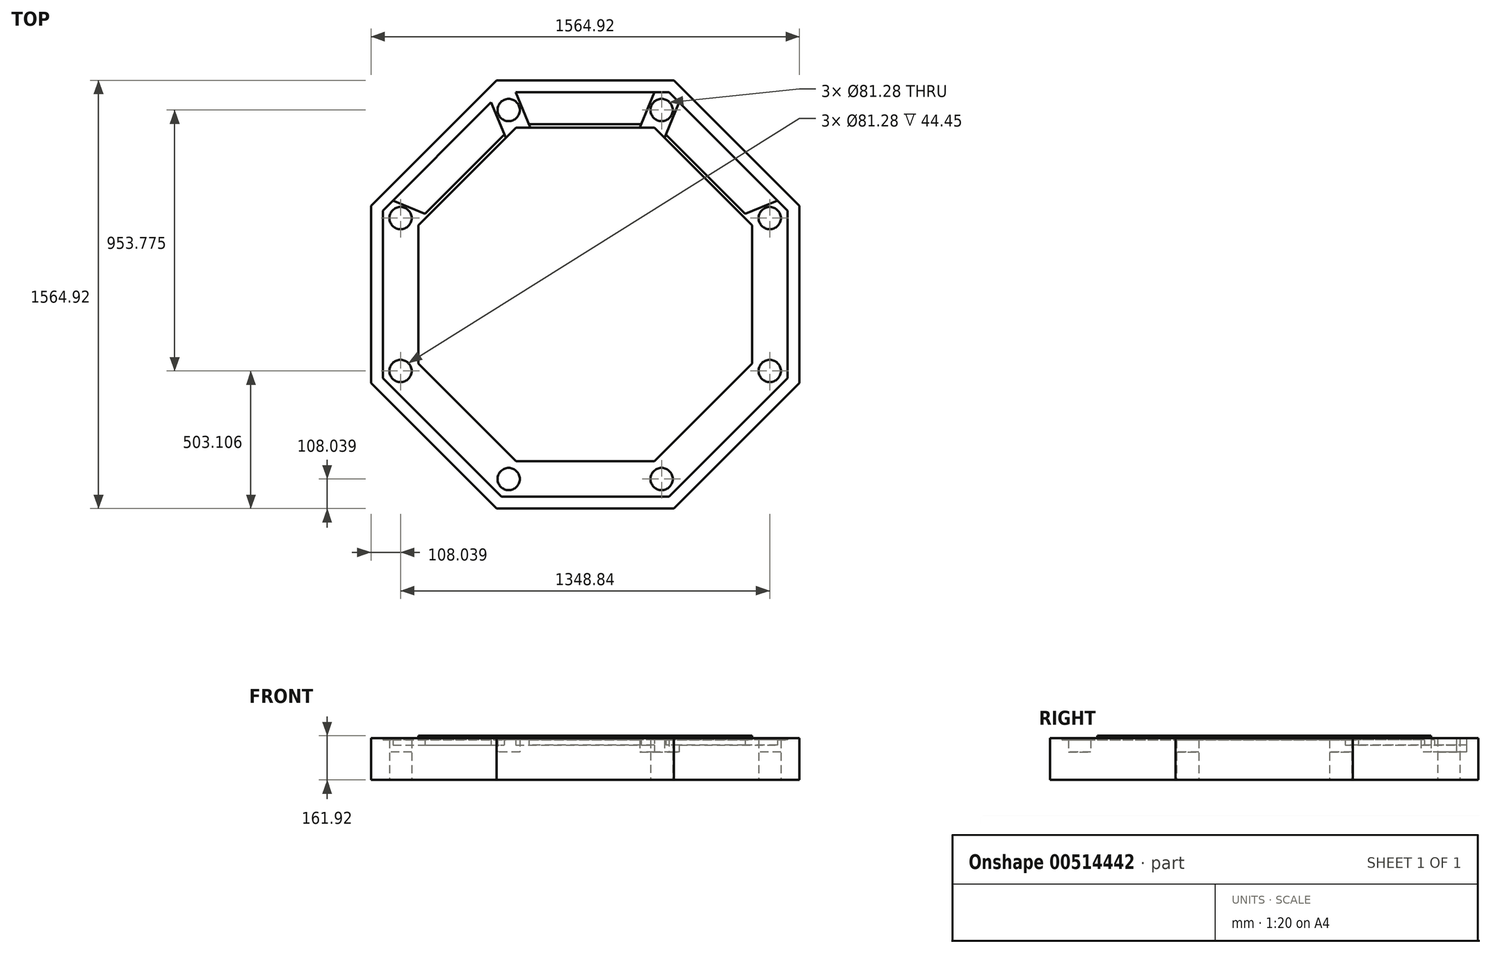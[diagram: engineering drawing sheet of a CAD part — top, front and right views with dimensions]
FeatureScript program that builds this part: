
annotation { "Feature Type Name" : "Feature", "Feature Type Description" : "" }
export const myFeature = defineFeature(function(context is Context, id is Id, definition is map)
    precondition{}
    {
        {
            var Q0;
            Q0=qCreatedBy(makeId("Top.planeOp"),FACE);
            var sketch = newSketch(context, id + "F0", { "sketchPlane" : qUnion([Q0])});
            skLineSegment(sketch, "E0.0", {"start": v(-324.1, 782.46) * mm, "end": v(324.1, 782.46) * mm});
            skLineSegment(sketch, "E0.1", {"start": v(324.1, 782.46) * mm, "end": v(782.46, 324.1) * mm});
            skLineSegment(sketch, "E0.2", {"start": v(782.46, 324.1) * mm, "end": v(782.46, -324.1) * mm});
            skLineSegment(sketch, "E0.3", {"start": v(782.46, -324.1) * mm, "end": v(324.1, -782.46) * mm});
            skLineSegment(sketch, "E0.4", {"start": v(324.1, -782.46) * mm, "end": v(-324.1, -782.46) * mm});
            skLineSegment(sketch, "E0.5", {"start": v(-324.1, -782.46) * mm, "end": v(-782.46, -324.1) * mm});
            skLineSegment(sketch, "E0.6", {"start": v(-782.46, -324.1) * mm, "end": v(-782.46, 324.1) * mm});
            skLineSegment(sketch, "E0.7", {"start": v(-782.46, 324.1) * mm, "end": v(-324.1, 782.46) * mm});
            skPoint(sketch, "E0.0.midPoint", {"position": v(0, 782.46) * mm});
            skLineSegment(sketch, "E1.0", {"start": v(-252.5, 609.6) * mm, "end": v(252.5, 609.6) * mm});
            skLineSegment(sketch, "E1.1", {"start": v(252.5, 609.6) * mm, "end": v(609.6, 252.5) * mm});
            skLineSegment(sketch, "E1.2", {"start": v(609.6, 252.5) * mm, "end": v(609.6, -252.5) * mm});
            skLineSegment(sketch, "E1.3", {"start": v(609.6, -252.5) * mm, "end": v(252.5, -609.6) * mm});
            skLineSegment(sketch, "E1.4", {"start": v(252.5, -609.6) * mm, "end": v(-252.5, -609.6) * mm});
            skLineSegment(sketch, "E1.5", {"start": v(-252.5, -609.6) * mm, "end": v(-609.6, -252.5) * mm});
            skLineSegment(sketch, "E1.6", {"start": v(-609.6, -252.5) * mm, "end": v(-609.6, 252.5) * mm});
            skLineSegment(sketch, "E1.7", {"start": v(-609.6, 252.5) * mm, "end": v(-252.5, 609.6) * mm});
            skPoint(sketch, "E1.0.midPoint", {"position": v(0, 609.6) * mm});
            skLineSegment(sketch, "E2.0", {"start": v(-306.2, 739.24) * mm, "end": v(306.2, 739.24) * mm});
            skLineSegment(sketch, "E2.1", {"start": v(306.2, 739.24) * mm, "end": v(739.24, 306.2) * mm});
            skLineSegment(sketch, "E2.2", {"start": v(739.24, 306.2) * mm, "end": v(739.24, -306.2) * mm});
            skLineSegment(sketch, "E2.3", {"start": v(739.24, -306.2) * mm, "end": v(306.2, -739.24) * mm});
            skLineSegment(sketch, "E2.4", {"start": v(306.2, -739.24) * mm, "end": v(-306.2, -739.24) * mm});
            skLineSegment(sketch, "E2.5", {"start": v(-306.2, -739.24) * mm, "end": v(-739.24, -306.2) * mm});
            skLineSegment(sketch, "E2.6", {"start": v(-739.24, -306.2) * mm, "end": v(-739.24, 306.2) * mm});
            skLineSegment(sketch, "E2.7", {"start": v(-739.24, 306.2) * mm, "end": v(-306.2, 739.24) * mm});
            skPoint(sketch, "E2.0.midPoint", {"position": v(0, 739.24) * mm});
            skLineSegment(sketch, "E3", {"start": v(-306.2, 739.24) * mm, "end": v(-252.5, 609.6) * mm, "construction": true});
            skLineSegment(sketch, "E4.0", {"start": v(-253.58, 739.24) * mm, "end": v(-199.88, 609.6) * mm});
            skLineSegment(sketch, "E5.0", {"start": v(-343.41, 702.03) * mm, "end": v(-289.71, 572.4) * mm});
            skLineSegment(sketch, "E6", {"start": v(0, 782.46) * mm, "end": v(0, -782.46) * mm, "construction": true});
            skCircle(sketch, "E7", {"center": v(-279.35, 674.42) * mm, "radius": 40.64 * mm});
            skLineSegment(sketch, "E8.MirrorCS", {"start": v(253.58, 739.24) * mm, "end": v(199.88, 609.6) * mm});
            skLineSegment(sketch, "E9.MirrorCS", {"start": v(343.41, 702.03) * mm, "end": v(289.71, 572.4) * mm});
            skCircle(sketch, "E10.MirrorC", {"center": v(279.35, 674.42) * mm, "radius": 40.64 * mm});
            skLineSegment(sketch, "E11", {"start": v(-782.46, 0) * mm, "end": v(782.46, 0) * mm, "construction": true});
            skLineSegment(sketch, "E12.MirrorCS", {"start": v(343.41, -702.03) * mm, "end": v(289.71, -572.4) * mm});
            skLineSegment(sketch, "E13.MirrorCS", {"start": v(253.58, -739.24) * mm, "end": v(199.88, -609.6) * mm});
            skCircle(sketch, "E14.MirrorC", {"center": v(279.35, -674.42) * mm, "radius": 40.64 * mm});
            skCircle(sketch, "E15.MirrorC", {"center": v(-279.35, -674.42) * mm, "radius": 40.64 * mm});
            skLineSegment(sketch, "E16.MirrorCS", {"start": v(-253.58, -739.24) * mm, "end": v(-199.88, -609.6) * mm});
            skLineSegment(sketch, "E17.MirrorCS", {"start": v(-343.41, -702.03) * mm, "end": v(-289.71, -572.4) * mm});
            skLineSegment(sketch, "E18", {"start": v(553.28, -553.28) * mm, "end": v(-553.28, 553.28) * mm, "construction": true});
            skLineSegment(sketch, "E19", {"start": v(553.28, 553.28) * mm, "end": v(-553.28, -553.28) * mm, "construction": true});
            skLineSegment(sketch, "E20.MirrorCS", {"start": v(702.03, 343.41) * mm, "end": v(572.4, 289.71) * mm});
            skLineSegment(sketch, "E21.MirrorCS", {"start": v(739.24, 253.58) * mm, "end": v(609.6, 199.88) * mm});
            skCircle(sketch, "E22.MirrorC", {"center": v(674.42, 279.35) * mm, "radius": 40.64 * mm});
            skLineSegment(sketch, "E23.MirrorCS", {"start": v(-739.24, -253.58) * mm, "end": v(-609.6, -199.88) * mm});
            skCircle(sketch, "E24.MirrorC", {"center": v(-674.42, -279.35) * mm, "radius": 40.64 * mm});
            skLineSegment(sketch, "E25.MirrorCS", {"start": v(-702.03, -343.41) * mm, "end": v(-572.4, -289.71) * mm});
            skLineSegment(sketch, "E26.MirrorCS", {"start": v(702.03, -343.41) * mm, "end": v(572.4, -289.71) * mm});
            skLineSegment(sketch, "E27.MirrorCS", {"start": v(739.24, -253.58) * mm, "end": v(609.6, -199.88) * mm});
            skCircle(sketch, "E28.MirrorC", {"center": v(674.42, -279.35) * mm, "radius": 40.64 * mm});
            skLineSegment(sketch, "E29.MirrorCS", {"start": v(-702.03, 343.41) * mm, "end": v(-572.4, 289.71) * mm});
            skLineSegment(sketch, "E30.MirrorCS", {"start": v(-739.24, 253.58) * mm, "end": v(-609.6, 199.88) * mm});
            skCircle(sketch, "E31.MirrorC", {"center": v(-674.42, 279.35) * mm, "radius": 40.64 * mm});
            skLineSegment(sketch, "E32.0", {"start": v(-205.14, 622.3) * mm, "end": v(205.14, 622.3) * mm});
            skLineSegment(sketch, "E33.MirrorCS", {"start": v(-205.14, -622.3) * mm, "end": v(205.14, -622.3) * mm});
            skLineSegment(sketch, "E34.MirrorCS", {"start": v(-622.3, -205.14) * mm, "end": v(-622.3, 205.14) * mm});
            skLineSegment(sketch, "E35.MirrorCS", {"start": v(622.3, -205.14) * mm, "end": v(622.3, 205.14) * mm});
            skLineSegment(sketch, "E36.0", {"start": v(294.97, 585.1) * mm, "end": v(585.1, 294.97) * mm});
            skLineSegment(sketch, "E37.MirrorCS", {"start": v(-585.1, -294.97) * mm, "end": v(-294.97, -585.1) * mm});
            skLineSegment(sketch, "E38.MirrorCS", {"start": v(-294.97, 585.1) * mm, "end": v(-585.1, 294.97) * mm});
            skLineSegment(sketch, "E39.MirrorCS", {"start": v(585.1, -294.97) * mm, "end": v(294.97, -585.1) * mm});
            skLineSegment(sketch, "E40", {"start": v(-585.1, 294.97) * mm, "end": v(-585.1, 294.97) * mm});
            skLineSegment(sketch, "E41", {"start": v(622.3, -205.14) * mm, "end": v(622.26, -205.13) * mm});
            skSolve(sketch);
        }
        {
            var Q0;
            Q0=makeQuery(id+"F0.imprint","IMPRINT",FACE,{"disambiguationData":[TD([[makeQuery(id+"F0.imprint","IMPRINT",EDGE,{"derivedFrom":sQuery(id+"F0.wireOp",EDGE,"E0.0")}),-1.0]])]});
            extrude(context, id + "F1", {"entities" : qUnion([Q0]), "endBound" : BoundingType.SYMMETRIC, "depth" : 152.4 * mm, "offsetDistance" : 25.4 * mm});
        }
        {
            var Q0;
            {var subQ0=sQuery(id+"F0.wireOp",EDGE,"E5.0");Q0=makeQuery(id+"F0.imprint","IMPRINT",FACE,{"disambiguationData":[TD([[makeQuery(id+"F0.imprint","IMPRINT",EDGE,{"derivedFrom":subQ0}),-1.0]])]});}
            var Q1;
            {var subQ0=sQuery(id+"F0.wireOp",EDGE,"E4.0");Q1=makeQuery(id+"F0.imprint","IMPRINT",FACE,{"disambiguationData":[TD([[makeQuery(id+"F0.imprint","IMPRINT",EDGE,{"derivedFrom":subQ0}),1.0]])]});}
            var Q2;
            {var subQ0=sQuery(id+"F0.wireOp",EDGE,"E9.MirrorCS");Q2=makeQuery(id+"F0.imprint","IMPRINT",FACE,{"disambiguationData":[TD([[makeQuery(id+"F0.imprint","IMPRINT",EDGE,{"derivedFrom":subQ0}),1.0]])]});}
            var Q3;
            {var subQ0=sQuery(id+"F0.wireOp",EDGE,"E23.MirrorCS");Q3=makeQuery(id+"F0.imprint","IMPRINT",FACE,{"disambiguationData":[TD([[makeQuery(id+"F0.imprint","IMPRINT",EDGE,{"derivedFrom":subQ0}),1.0]])]});}
            var Q4;
            {var subQ0=sQuery(id+"F0.wireOp",EDGE,"E21.MirrorCS");Q4=makeQuery(id+"F0.imprint","IMPRINT",FACE,{"disambiguationData":[TD([[makeQuery(id+"F0.imprint","IMPRINT",EDGE,{"derivedFrom":subQ0}),1.0]])]});}
            var Q5;
            {var subQ0=sQuery(id+"F0.wireOp",EDGE,"E12.MirrorCS");Q5=makeQuery(id+"F0.imprint","IMPRINT",FACE,{"disambiguationData":[TD([[makeQuery(id+"F0.imprint","IMPRINT",EDGE,{"derivedFrom":subQ0}),-1.0]])]});}
            var Q6;
            {var subQ0=sQuery(id+"F0.wireOp",EDGE,"E13.MirrorCS");Q6=makeQuery(id+"F0.imprint","IMPRINT",FACE,{"disambiguationData":[TD([[makeQuery(id+"F0.imprint","IMPRINT",EDGE,{"derivedFrom":subQ0}),1.0]])]});}
            var Q7;
            {var subQ0=sQuery(id+"F0.wireOp",EDGE,"E17.MirrorCS");Q7=makeQuery(id+"F0.imprint","IMPRINT",FACE,{"disambiguationData":[TD([[makeQuery(id+"F0.imprint","IMPRINT",EDGE,{"derivedFrom":subQ0}),1.0]])]});}
            extrude(context, id + "F2", {"entities" : qUnion([Q0, Q1, Q2, Q3, Q4, Q5, Q6, Q7]), "operationType" : NewBodyOperationType.ADD, "endBound" : BoundingType.SYMMETRIC, "depth" : 127 * mm});
        }
        {
            var Q0;
            Q0=makeQuery(id+"F2.opExtrude","CAP_FACE",FACE,{"disambiguationData":[OSD([sQuery(id+"F0.wireOp",EDGE,"E1.3"),sQuery(id+"F0.wireOp",EDGE,"E2.3"),sQuery(id+"F0.wireOp",EDGE,"E12.MirrorCS"),sQuery(id+"F0.wireOp",EDGE,"E26.MirrorCS")])],"isStart":true});
            var Q1;
            Q1=makeQuery(id+"F2.opExtrude","CAP_FACE",FACE,{"disambiguationData":[OSD([sQuery(id+"F0.wireOp",EDGE,"E1.4"),sQuery(id+"F0.wireOp",EDGE,"E2.4"),sQuery(id+"F0.wireOp",EDGE,"E13.MirrorCS"),sQuery(id+"F0.wireOp",EDGE,"E16.MirrorCS")])],"isStart":true});
            var Q2;
            Q2=makeQuery(id+"F2.opExtrude","CAP_FACE",FACE,{"disambiguationData":[OSD([sQuery(id+"F0.wireOp",EDGE,"E1.5"),sQuery(id+"F0.wireOp",EDGE,"E2.5"),sQuery(id+"F0.wireOp",EDGE,"E17.MirrorCS"),sQuery(id+"F0.wireOp",EDGE,"E25.MirrorCS")])],"isStart":true});
            var Q3;
            Q3=makeQuery(id+"F2.opExtrude","CAP_FACE",FACE,{"disambiguationData":[OSD([sQuery(id+"F0.wireOp",EDGE,"E1.6"),sQuery(id+"F0.wireOp",EDGE,"E2.6"),sQuery(id+"F0.wireOp",EDGE,"E23.MirrorCS"),sQuery(id+"F0.wireOp",EDGE,"E30.MirrorCS")])],"isStart":true});
            var Q4;
            Q4=makeQuery(id+"F2.opExtrude","CAP_FACE",FACE,{"disambiguationData":[OSD([sQuery(id+"F0.wireOp",EDGE,"E1.7"),sQuery(id+"F0.wireOp",EDGE,"E2.7"),sQuery(id+"F0.wireOp",EDGE,"E5.0"),sQuery(id+"F0.wireOp",EDGE,"E29.MirrorCS")])],"isStart":true});
            var Q5;
            Q5=makeQuery(id+"F2.opExtrude","CAP_FACE",FACE,{"disambiguationData":[OSD([sQuery(id+"F0.wireOp",EDGE,"E1.0"),sQuery(id+"F0.wireOp",EDGE,"E2.0"),sQuery(id+"F0.wireOp",EDGE,"E4.0"),sQuery(id+"F0.wireOp",EDGE,"E8.MirrorCS")])],"isStart":true});
            var Q6;
            Q6=makeQuery(id+"F2.opExtrude","CAP_FACE",FACE,{"disambiguationData":[OSD([sQuery(id+"F0.wireOp",EDGE,"E1.1"),sQuery(id+"F0.wireOp",EDGE,"E2.1"),sQuery(id+"F0.wireOp",EDGE,"E9.MirrorCS"),sQuery(id+"F0.wireOp",EDGE,"E20.MirrorCS")])],"isStart":true});
            var Q7;
            Q7=makeQuery(id+"F2.opExtrude","CAP_FACE",FACE,{"disambiguationData":[OSD([sQuery(id+"F0.wireOp",EDGE,"E1.2"),sQuery(id+"F0.wireOp",EDGE,"E2.2"),sQuery(id+"F0.wireOp",EDGE,"E21.MirrorCS"),sQuery(id+"F0.wireOp",EDGE,"E27.MirrorCS")])],"isStart":true});
            extrude(context, id + "F3", {"entities" : qUnion([Q0, Q1, Q2, Q3, Q4, Q5, Q6, Q7]), "operationType" : NewBodyOperationType.ADD, "depth" : 12.7 * mm});
        }
        {
            var Q0;
            {var subQ4=sQuery(id+"F0.wireOp",EDGE,"E4.0");Q0=makeQuery(id+"F0.imprint","IMPRINT",FACE,{"disambiguationData":[TD([[makeQuery(id+"F0.imprint","IMPRINT",EDGE,{"derivedFrom":subQ4}),-1.0]])]});}
            var Q1;
            {var subQ3=sQuery(id+"F0.wireOp",EDGE,"E8.MirrorCS");Q1=makeQuery(id+"F0.imprint","IMPRINT",FACE,{"disambiguationData":[TD([[makeQuery(id+"F0.imprint","IMPRINT",EDGE,{"derivedFrom":subQ3}),1.0]])]});}
            var Q2;
            {var subQ7=sQuery(id+"F0.wireOp",EDGE,"E29.MirrorCS");Q2=makeQuery(id+"F0.imprint","IMPRINT",FACE,{"disambiguationData":[TD([[makeQuery(id+"F0.imprint","IMPRINT",EDGE,{"derivedFrom":subQ7}),-1.0]])]});}
            var Q3;
            {var subQ4=sQuery(id+"F0.wireOp",EDGE,"E23.MirrorCS");Q3=makeQuery(id+"F0.imprint","IMPRINT",FACE,{"disambiguationData":[TD([[makeQuery(id+"F0.imprint","IMPRINT",EDGE,{"derivedFrom":subQ4}),-1.0]])]});}
            var Q4;
            {var subQ3=sQuery(id+"F0.wireOp",EDGE,"E20.MirrorCS");Q4=makeQuery(id+"F0.imprint","IMPRINT",FACE,{"disambiguationData":[TD([[makeQuery(id+"F0.imprint","IMPRINT",EDGE,{"derivedFrom":subQ3}),1.0]])]});}
            var Q5;
            {var subQ7=sQuery(id+"F0.wireOp",EDGE,"E26.MirrorCS");Q5=makeQuery(id+"F0.imprint","IMPRINT",FACE,{"disambiguationData":[TD([[makeQuery(id+"F0.imprint","IMPRINT",EDGE,{"derivedFrom":subQ7}),-1.0]])]});}
            var Q6;
            Q6=makeQuery(id+"F0.imprint","IMPRINT",FACE,{"disambiguationData":[TD([[makeQuery(id+"F0.imprint","IMPRINT",EDGE,{"derivedFrom":sQuery(id+"F0.wireOp",EDGE,"E15.MirrorC")}),1.0]])]});
            var Q7;
            {var subQ3=sQuery(id+"F0.wireOp",EDGE,"E12.MirrorCS");Q7=makeQuery(id+"F0.imprint","IMPRINT",FACE,{"disambiguationData":[TD([[makeQuery(id+"F0.imprint","IMPRINT",EDGE,{"derivedFrom":subQ3}),1.0]])]});}
            var Q8;
            Q8=makeQuery(id+"F0.imprint","IMPRINT",FACE,{"disambiguationData":[TD([[makeQuery(id+"F0.imprint","IMPRINT",EDGE,{"derivedFrom":sQuery(id+"F0.wireOp",EDGE,"E22.MirrorC")}),1.0]])]});
            var Q9;
            Q9=makeQuery(id+"F0.imprint","IMPRINT",FACE,{"disambiguationData":[TD([[makeQuery(id+"F0.imprint","IMPRINT",EDGE,{"derivedFrom":sQuery(id+"F0.wireOp",EDGE,"E10.MirrorC")}),-1.0]])]});
            var Q10;
            Q10=makeQuery(id+"F0.imprint","IMPRINT",FACE,{"disambiguationData":[TD([[makeQuery(id+"F0.imprint","IMPRINT",EDGE,{"derivedFrom":sQuery(id+"F0.wireOp",EDGE,"E7")}),1.0]])]});
            var Q11;
            Q11=makeQuery(id+"F0.imprint","IMPRINT",FACE,{"disambiguationData":[TD([[makeQuery(id+"F0.imprint","IMPRINT",EDGE,{"derivedFrom":sQuery(id+"F0.wireOp",EDGE,"E31.MirrorC")}),-1.0]])]});
            var Q12;
            Q12=makeQuery(id+"F0.imprint","IMPRINT",FACE,{"disambiguationData":[TD([[makeQuery(id+"F0.imprint","IMPRINT",EDGE,{"derivedFrom":sQuery(id+"F0.wireOp",EDGE,"E24.MirrorC")}),1.0]])]});
            var Q13;
            Q13=makeQuery(id+"F0.imprint","IMPRINT",FACE,{"disambiguationData":[TD([[makeQuery(id+"F0.imprint","IMPRINT",EDGE,{"derivedFrom":sQuery(id+"F0.wireOp",EDGE,"E15.MirrorC")}),-1.0]])]});
            var Q14;
            Q14=makeQuery(id+"F0.imprint","IMPRINT",FACE,{"disambiguationData":[TD([[makeQuery(id+"F0.imprint","IMPRINT",EDGE,{"derivedFrom":sQuery(id+"F0.wireOp",EDGE,"E14.MirrorC")}),1.0]])]});
            var Q15;
            Q15=makeQuery(id+"F0.imprint","IMPRINT",FACE,{"disambiguationData":[TD([[makeQuery(id+"F0.imprint","IMPRINT",EDGE,{"derivedFrom":sQuery(id+"F0.wireOp",EDGE,"E28.MirrorC")}),-1.0]])]});
            extrude(context, id + "F4", {"entities" : qUnion([Q0, Q1, Q2, Q3, Q4, Q5, Q6, Q7, Q8, Q9, Q10, Q11, Q12, Q13, Q14, Q15]), "operationType" : NewBodyOperationType.ADD, "endBound" : BoundingType.SYMMETRIC, "depth" : 152.4 * mm});
        }
        {
            var Q0;
            Q0=makeQuery(id+"F0.imprint","IMPRINT",FACE,{"disambiguationData":[TD([[makeQuery(id+"F0.imprint","IMPRINT",EDGE,{"derivedFrom":sQuery(id+"F0.wireOp",EDGE,"E31.MirrorC")}),-1.0]])]});
            var Q1;
            Q1=makeQuery(id+"F0.imprint","IMPRINT",FACE,{"disambiguationData":[TD([[makeQuery(id+"F0.imprint","IMPRINT",EDGE,{"derivedFrom":sQuery(id+"F0.wireOp",EDGE,"E7")}),1.0]])]});
            var Q2;
            Q2=makeQuery(id+"F0.imprint","IMPRINT",FACE,{"disambiguationData":[TD([[makeQuery(id+"F0.imprint","IMPRINT",EDGE,{"derivedFrom":sQuery(id+"F0.wireOp",EDGE,"E10.MirrorC")}),-1.0]])]});
            var Q3;
            Q3=makeQuery(id+"F0.imprint","IMPRINT",FACE,{"disambiguationData":[TD([[makeQuery(id+"F0.imprint","IMPRINT",EDGE,{"derivedFrom":sQuery(id+"F0.wireOp",EDGE,"E22.MirrorC")}),1.0]])]});
            var Q4;
            Q4=makeQuery(id+"F0.imprint","IMPRINT",FACE,{"disambiguationData":[TD([[makeQuery(id+"F0.imprint","IMPRINT",EDGE,{"derivedFrom":sQuery(id+"F0.wireOp",EDGE,"E28.MirrorC")}),-1.0]])]});
            var Q5;
            Q5=makeQuery(id+"F0.imprint","IMPRINT",FACE,{"disambiguationData":[TD([[makeQuery(id+"F0.imprint","IMPRINT",EDGE,{"derivedFrom":sQuery(id+"F0.wireOp",EDGE,"E14.MirrorC")}),1.0]])]});
            var Q6;
            Q6=makeQuery(id+"F0.imprint","IMPRINT",FACE,{"disambiguationData":[TD([[makeQuery(id+"F0.imprint","IMPRINT",EDGE,{"derivedFrom":sQuery(id+"F0.wireOp",EDGE,"E15.MirrorC")}),-1.0]])]});
            var Q7;
            Q7=makeQuery(id+"F0.imprint","IMPRINT",FACE,{"disambiguationData":[TD([[makeQuery(id+"F0.imprint","IMPRINT",EDGE,{"derivedFrom":sQuery(id+"F0.wireOp",EDGE,"E24.MirrorC")}),1.0]])]});
            extrude(context, id + "F5", {"entities" : qUnion([Q0, Q1, Q2, Q3, Q4, Q5, Q6, Q7]), "operationType" : NewBodyOperationType.REMOVE, "endBound" : BoundingType.THROUGH_ALL, "depth" : 50.8 * mm});
        }
        {
            var Q0;
            Q0=makeQuery(id+"F0.imprint","IMPRINT",FACE,{"disambiguationData":[TD([[makeQuery(id+"F0.imprint","IMPRINT",EDGE,{"derivedFrom":sQuery(id+"F0.wireOp",EDGE,"E7")}),1.0]])]});
            var Q1;
            Q1=makeQuery(id+"F0.imprint","IMPRINT",FACE,{"disambiguationData":[TD([[makeQuery(id+"F0.imprint","IMPRINT",EDGE,{"derivedFrom":sQuery(id+"F0.wireOp",EDGE,"E10.MirrorC")}),-1.0]])]});
            var Q2;
            Q2=makeQuery(id+"F0.imprint","IMPRINT",FACE,{"disambiguationData":[TD([[makeQuery(id+"F0.imprint","IMPRINT",EDGE,{"derivedFrom":sQuery(id+"F0.wireOp",EDGE,"E22.MirrorC")}),1.0]])]});
            var Q3;
            Q3=makeQuery(id+"F0.imprint","IMPRINT",FACE,{"disambiguationData":[TD([[makeQuery(id+"F0.imprint","IMPRINT",EDGE,{"derivedFrom":sQuery(id+"F0.wireOp",EDGE,"E28.MirrorC")}),-1.0]])]});
            var Q4;
            Q4=makeQuery(id+"F0.imprint","IMPRINT",FACE,{"disambiguationData":[TD([[makeQuery(id+"F0.imprint","IMPRINT",EDGE,{"derivedFrom":sQuery(id+"F0.wireOp",EDGE,"E14.MirrorC")}),1.0]])]});
            var Q5;
            Q5=makeQuery(id+"F0.imprint","IMPRINT",FACE,{"disambiguationData":[TD([[makeQuery(id+"F0.imprint","IMPRINT",EDGE,{"derivedFrom":sQuery(id+"F0.wireOp",EDGE,"E15.MirrorC")}),-1.0]])]});
            var Q6;
            Q6=makeQuery(id+"F0.imprint","IMPRINT",FACE,{"disambiguationData":[TD([[makeQuery(id+"F0.imprint","IMPRINT",EDGE,{"derivedFrom":sQuery(id+"F0.wireOp",EDGE,"E24.MirrorC")}),1.0]])]});
            var Q7;
            Q7=makeQuery(id+"F0.imprint","IMPRINT",FACE,{"disambiguationData":[TD([[makeQuery(id+"F0.imprint","IMPRINT",EDGE,{"derivedFrom":sQuery(id+"F0.wireOp",EDGE,"E31.MirrorC")}),-1.0]])]});
            extrude(context, id + "F6", {"entities" : qUnion([Q0, Q1, Q2, Q3, Q4, Q5, Q6, Q7]), "operationType" : NewBodyOperationType.ADD, "depth" : 25.4 * mm});
        }
        {
            var Q0;
            {var subQ0=sQuery(id+"F0.wireOp",EDGE,"E1.7");var subQ19=sQuery(id+"F0.wireOp",EDGE,"E1.0");var subQ24=makeQuery(id+"F0.imprint","INTERSECT",VERTEX,{"derivedFrom":[subQ19,subQ0]});Q0=makeQuery(id+"F0.imprint","IMPRINT",FACE,{"disambiguationData":[TD([[makeQuery(id+"F0.imprint","IMPRINT",EDGE,{"disambiguationData":[TD([[subQ24,-1.0]])],"derivedFrom":subQ19}),-1.0]])]});}
            extrude(context, id + "F7", {"entities" : qUnion([Q0]), "operationType" : NewBodyOperationType.ADD, "oppositeDirection" : true, "depth" : 76.2 * mm});
        }
        {
            var Q0;
            {var subQ0=sQuery(id+"F0.wireOp",EDGE,"E1.7");var subQ19=sQuery(id+"F0.wireOp",EDGE,"E1.0");var subQ24=makeQuery(id+"F0.imprint","INTERSECT",VERTEX,{"derivedFrom":[subQ19,subQ0]});Q0=makeQuery(id+"F0.imprint","IMPRINT",FACE,{"disambiguationData":[TD([[makeQuery(id+"F0.imprint","IMPRINT",EDGE,{"disambiguationData":[TD([[subQ24,-1.0]])],"derivedFrom":subQ19}),-1.0]])]});}
            extrude(context, id + "F8", {"entities" : qUnion([Q0]), "operationType" : NewBodyOperationType.ADD, "depth" : 82.55 * mm});
        }
        {
            var Q0;
            Q0=makeQuery(id+"F2.opExtrude","CAP_FACE",FACE,{"disambiguationData":[OSD([sQuery(id+"F0.wireOp",EDGE,"E1.4"),sQuery(id+"F0.wireOp",EDGE,"E2.4"),sQuery(id+"F0.wireOp",EDGE,"E13.MirrorCS"),sQuery(id+"F0.wireOp",EDGE,"E16.MirrorCS")])],"isStart":false});
            var Q1;
            Q1=makeQuery(id+"F2.opExtrude","CAP_FACE",FACE,{"disambiguationData":[OSD([sQuery(id+"F0.wireOp",EDGE,"E1.3"),sQuery(id+"F0.wireOp",EDGE,"E2.3"),sQuery(id+"F0.wireOp",EDGE,"E12.MirrorCS"),sQuery(id+"F0.wireOp",EDGE,"E26.MirrorCS")])],"isStart":false});
            var Q2;
            Q2=makeQuery(id+"F2.opExtrude","CAP_FACE",FACE,{"disambiguationData":[OSD([sQuery(id+"F0.wireOp",EDGE,"E1.2"),sQuery(id+"F0.wireOp",EDGE,"E2.2"),sQuery(id+"F0.wireOp",EDGE,"E21.MirrorCS"),sQuery(id+"F0.wireOp",EDGE,"E27.MirrorCS")])],"isStart":false});
            var Q3;
            Q3=makeQuery(id+"F2.opExtrude","CAP_FACE",FACE,{"disambiguationData":[OSD([sQuery(id+"F0.wireOp",EDGE,"E1.1"),sQuery(id+"F0.wireOp",EDGE,"E2.1"),sQuery(id+"F0.wireOp",EDGE,"E9.MirrorCS"),sQuery(id+"F0.wireOp",EDGE,"E20.MirrorCS")])],"isStart":false});
            var Q4;
            Q4=makeQuery(id+"F2.opExtrude","CAP_FACE",FACE,{"disambiguationData":[OSD([sQuery(id+"F0.wireOp",EDGE,"E1.0"),sQuery(id+"F0.wireOp",EDGE,"E2.0"),sQuery(id+"F0.wireOp",EDGE,"E4.0"),sQuery(id+"F0.wireOp",EDGE,"E8.MirrorCS")])],"isStart":false});
            var Q5;
            Q5=makeQuery(id+"F2.opExtrude","CAP_FACE",FACE,{"disambiguationData":[OSD([sQuery(id+"F0.wireOp",EDGE,"E1.7"),sQuery(id+"F0.wireOp",EDGE,"E2.7"),sQuery(id+"F0.wireOp",EDGE,"E5.0"),sQuery(id+"F0.wireOp",EDGE,"E29.MirrorCS")])],"isStart":false});
            var Q6;
            Q6=makeQuery(id+"F2.opExtrude","CAP_FACE",FACE,{"disambiguationData":[OSD([sQuery(id+"F0.wireOp",EDGE,"E1.6"),sQuery(id+"F0.wireOp",EDGE,"E2.6"),sQuery(id+"F0.wireOp",EDGE,"E23.MirrorCS"),sQuery(id+"F0.wireOp",EDGE,"E30.MirrorCS")])],"isStart":false});
            var Q7;
            Q7=makeQuery(id+"F2.opExtrude","CAP_FACE",FACE,{"disambiguationData":[OSD([sQuery(id+"F0.wireOp",EDGE,"E1.5"),sQuery(id+"F0.wireOp",EDGE,"E2.5"),sQuery(id+"F0.wireOp",EDGE,"E17.MirrorCS"),sQuery(id+"F0.wireOp",EDGE,"E25.MirrorCS")])],"isStart":false});
            extrude(context, id + "F9", {"entities" : qUnion([Q0, Q1, Q2, Q3, Q4, Q5, Q6, Q7]), "operationType" : NewBodyOperationType.REMOVE, "oppositeDirection" : true, "depth" : 12.7 * mm, "offsetDistance" : 25.4 * mm});
        }
        {
            var Q0;
            Q0=makeQuery(id+"F8.opExtrude","CAP_FACE",FACE,{"disambiguationData":[OSD([sQuery(id+"F0.wireOp",EDGE,"E1.0"),sQuery(id+"F0.wireOp",EDGE,"E1.1"),sQuery(id+"F0.wireOp",EDGE,"E1.2"),sQuery(id+"F0.wireOp",EDGE,"E1.3"),sQuery(id+"F0.wireOp",EDGE,"E1.4"),sQuery(id+"F0.wireOp",EDGE,"E1.5"),sQuery(id+"F0.wireOp",EDGE,"E1.6"),sQuery(id+"F0.wireOp",EDGE,"E1.7")])],"isStart":false});
            extrude(context, id + "F10", {"entities" : qUnion([Q0]), "operationType" : NewBodyOperationType.ADD, "depth" : 3.17 * mm, "offsetDistance" : 25.4 * mm});
        }
        {
            var Q0;
            {var subQ0=sQuery(id+"F0.wireOp",EDGE,"E35.MirrorCS");Q0=makeQuery(id+"F0.imprint","IMPRINT",FACE,{"disambiguationData":[TD([[makeQuery(id+"F0.imprint","IMPRINT",EDGE,{"derivedFrom":subQ0}),1.0]])]});}
            var Q1;
            {var subQ5=sQuery(id+"F0.wireOp",EDGE,"E36.0");Q1=makeQuery(id+"F0.imprint","IMPRINT",FACE,{"disambiguationData":[TD([[makeQuery(id+"F0.imprint","IMPRINT",EDGE,{"derivedFrom":subQ5}),-1.0]])]});}
            var Q2;
            {var subQ5=sQuery(id+"F0.wireOp",EDGE,"E32.0");Q2=makeQuery(id+"F0.imprint","IMPRINT",FACE,{"disambiguationData":[TD([[makeQuery(id+"F0.imprint","IMPRINT",EDGE,{"derivedFrom":subQ5}),-1.0]])]});}
            var Q3;
            {var subQ0=sQuery(id+"F0.wireOp",EDGE,"E38.MirrorCS");Q3=makeQuery(id+"F0.imprint","IMPRINT",FACE,{"disambiguationData":[TD([[makeQuery(id+"F0.imprint","IMPRINT",EDGE,{"derivedFrom":subQ0}),1.0]])]});}
            var Q4;
            {var subQ0=sQuery(id+"F0.wireOp",EDGE,"E23.MirrorCS");var subQ1=sQuery(id+"F0.wireOp",EDGE,"E1.6");var subQ2=makeQuery(id+"F0.imprint","INTERSECT",VERTEX,{"derivedFrom":[subQ1,subQ0]});Q4=makeQuery(id+"F0.imprint","IMPRINT",FACE,{"disambiguationData":[TD([[makeQuery(id+"F0.imprint","IMPRINT",EDGE,{"disambiguationData":[TD([[subQ2,-1.0]])],"derivedFrom":subQ1}),1.0]])]});}
            var Q5;
            {var subQ5=sQuery(id+"F0.wireOp",EDGE,"E37.MirrorCS");Q5=makeQuery(id+"F0.imprint","IMPRINT",FACE,{"disambiguationData":[TD([[makeQuery(id+"F0.imprint","IMPRINT",EDGE,{"derivedFrom":subQ5}),1.0]])]});}
            var Q6;
            {var subQ5=sQuery(id+"F0.wireOp",EDGE,"E33.MirrorCS");Q6=makeQuery(id+"F0.imprint","IMPRINT",FACE,{"disambiguationData":[TD([[makeQuery(id+"F0.imprint","IMPRINT",EDGE,{"derivedFrom":subQ5}),1.0]])]});}
            var Q7;
            {var subQ0=sQuery(id+"F0.wireOp",EDGE,"E12.MirrorCS");var subQ1=sQuery(id+"F0.wireOp",EDGE,"E1.3");var subQ2=makeQuery(id+"F0.imprint","INTERSECT",VERTEX,{"derivedFrom":[subQ1,subQ0]});Q7=makeQuery(id+"F0.imprint","IMPRINT",FACE,{"disambiguationData":[TD([[makeQuery(id+"F0.imprint","IMPRINT",EDGE,{"disambiguationData":[TD([[subQ2,1.0]])],"derivedFrom":subQ1}),1.0]])]});}
            extrude(context, id + "F11", {"entities" : qUnion([Q0, Q1, Q2, Q3, Q4, Q5, Q6, Q7]), "operationType" : NewBodyOperationType.ADD, "depth" : 69.85 * mm, "offsetDistance" : 25.4 * mm});
        }
    });
